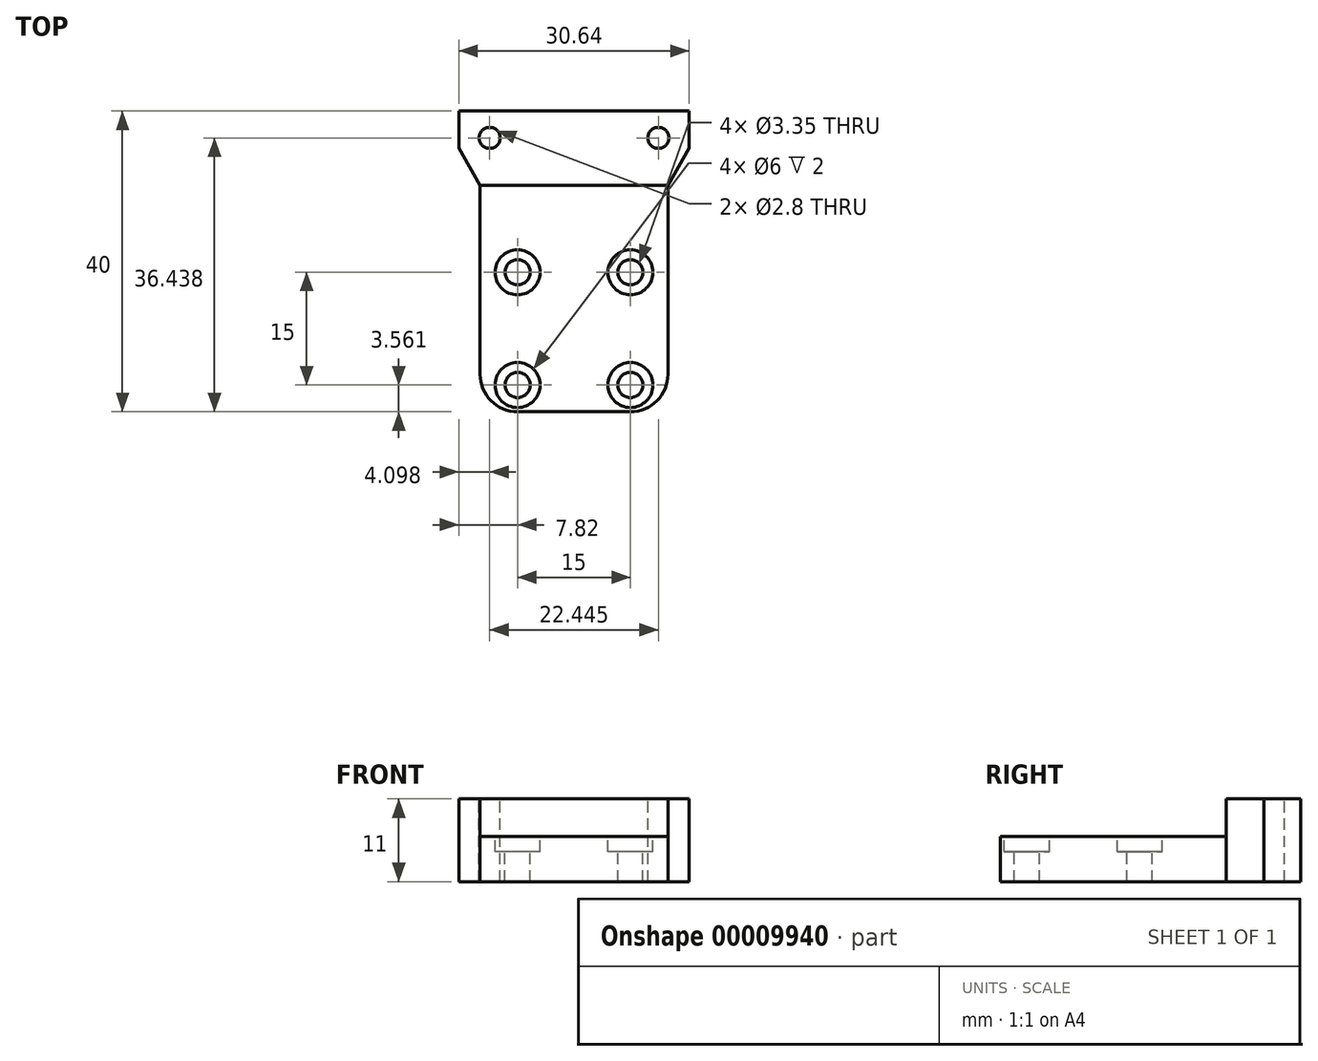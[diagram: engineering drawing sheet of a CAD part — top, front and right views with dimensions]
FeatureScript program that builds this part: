
annotation { "Feature Type Name" : "Feature", "Feature Type Description" : "" }
export const myFeature = defineFeature(function(context is Context, id is Id, definition is map)
    precondition{}
    {
        {
            var Q0;
            Q0=qCreatedBy(makeId("Top.planeOp"),FACE);
            var sketch = newSketch(context, id + "F0", { "sketchPlane" : qUnion([Q0])});
            skLineSegment(sketch, "E0.bottom", {"start": v(0, 0) * mm, "end": v(25, 0) * mm});
            skLineSegment(sketch, "E0.top", {"start": v(-2.82, 40) * mm, "end": v(27.82, 40) * mm});
            skLineSegment(sketch, "E1", {"start": v(0, 30.1) * mm, "end": v(25, 30.1) * mm});
            skLineSegment(sketch, "E2", {"start": v(-2.82, 35.1) * mm, "end": v(27.82, 35.1) * mm});
            skLineSegment(sketch, "E3", {"start": v(0, 0) * mm, "end": v(0, 30.1) * mm});
            skLineSegment(sketch, "E4", {"start": v(0, 30.1) * mm, "end": v(-2.82, 35.1) * mm});
            skLineSegment(sketch, "E5", {"start": v(-2.82, 35.1) * mm, "end": v(-2.82, 40) * mm});
            skLineSegment(sketch, "E6", {"start": v(25, 0) * mm, "end": v(25, 30.1) * mm});
            skLineSegment(sketch, "E7", {"start": v(25, 30.1) * mm, "end": v(27.82, 35.1) * mm});
            skLineSegment(sketch, "E8", {"start": v(27.82, 35.1) * mm, "end": v(27.82, 40) * mm});
            skSolve(sketch);
        }
        {
            var Q0;
            Q0=qSketchRegion(id+"F0",true);
            extrude(context, id + "F1", {"entities" : qUnion([Q0]), "depth" : 6 * mm});
        }
        {
            var Q0;
            Q0=makeQuery(id+"F1.opExtrude","CAP_FACE",FACE,{"disambiguationData":[OSD([sQuery(id+"F0.wireOp",EDGE,"E0.bottom"),sQuery(id+"F0.wireOp",EDGE,"E0.top"),sQuery(id+"F0.wireOp",EDGE,"E3"),sQuery(id+"F0.wireOp",EDGE,"E4"),sQuery(id+"F0.wireOp",EDGE,"E5"),sQuery(id+"F0.wireOp",EDGE,"E6"),sQuery(id+"F0.wireOp",EDGE,"E7"),sQuery(id+"F0.wireOp",EDGE,"E8")])],"isStart":false});
            var sketch = newSketch(context, id + "F2", { "sketchPlane" : qUnion([Q0])});
            skCircle(sketch, "E9", {"center": v(5, 18.56) * mm, "radius": 1.68 * mm});
            skCircle(sketch, "E10", {"center": v(20, 18.56) * mm, "radius": 1.68 * mm});
            skCircle(sketch, "E11", {"center": v(5, 3.56) * mm, "radius": 1.68 * mm});
            skCircle(sketch, "E12", {"center": v(20, 3.56) * mm, "radius": 1.68 * mm});
            skLineSegment(sketch, "E13", {"start": v(5, 18.56) * mm, "end": v(0, 18.56) * mm});
            skLineSegment(sketch, "E14", {"start": v(20, 3.56) * mm, "end": v(25, 3.56) * mm});
            skCircle(sketch, "E15", {"center": v(5, 18.56) * mm, "radius": 3 * mm});
            skCircle(sketch, "E16", {"center": v(20, 18.56) * mm, "radius": 3 * mm});
            skCircle(sketch, "E17", {"center": v(5, 3.56) * mm, "radius": 3 * mm});
            skCircle(sketch, "E18", {"center": v(20, 3.56) * mm, "radius": 3 * mm});
            skSolve(sketch);
        }
        {
            var Q0;
            Q0=makeQuery(id+"F2.imprint","IMPRINT",FACE,{"disambiguationData":[TD([[makeQuery(id+"F2.imprint","IMPRINT",EDGE,{"derivedFrom":sQuery(id+"F2.wireOp",EDGE,"E9")}),1.0]])]});
            var Q1;
            Q1=makeQuery(id+"F2.imprint","IMPRINT",FACE,{"disambiguationData":[TD([[makeQuery(id+"F2.imprint","IMPRINT",EDGE,{"derivedFrom":sQuery(id+"F2.wireOp",EDGE,"E10")}),1.0]])]});
            var Q2;
            Q2=makeQuery(id+"F2.imprint","IMPRINT",FACE,{"disambiguationData":[TD([[makeQuery(id+"F2.imprint","IMPRINT",EDGE,{"derivedFrom":sQuery(id+"F2.wireOp",EDGE,"E12")}),1.0]])]});
            var Q3;
            Q3=makeQuery(id+"F2.imprint","IMPRINT",FACE,{"disambiguationData":[TD([[makeQuery(id+"F2.imprint","IMPRINT",EDGE,{"derivedFrom":sQuery(id+"F2.wireOp",EDGE,"E11")}),1.0]])]});
            var Q4;
            Q4=makeQuery(id+"F2.imprint","IMPRINT",FACE,{"disambiguationData":[TD([[makeQuery(id+"F2.imprint","IMPRINT",EDGE,{"derivedFrom":sQuery(id+"F2.wireOp",EDGE,"97d24b09-4827-4c46-a1fd-a3ea8677536d")}),1.0]])]});
            var Q5;
            Q5=makeQuery(id+"F2.imprint","IMPRINT",FACE,{"disambiguationData":[TD([[makeQuery(id+"F2.imprint","IMPRINT",EDGE,{"derivedFrom":sQuery(id+"F2.wireOp",EDGE,"b6eb7b6f-8bb0-4363-9520-a6d7085f5256")}),1.0]])]});
            extrude(context, id + "F3", {"entities" : qUnion([Q0, Q1, Q2, Q3, Q4, Q5]), "operationType" : NewBodyOperationType.REMOVE, "oppositeDirection" : true, "depth" : 25 * mm});
        }
        {
            var Q0;
            Q0=makeQuery(id+"F2.imprint","IMPRINT",FACE,{"disambiguationData":[TD([[makeQuery(id+"F2.imprint","IMPRINT",EDGE,{"derivedFrom":sQuery(id+"F2.wireOp",EDGE,"E9")}),-1.0]])]});
            var Q1;
            Q1=makeQuery(id+"F2.imprint","IMPRINT",FACE,{"disambiguationData":[TD([[makeQuery(id+"F2.imprint","IMPRINT",EDGE,{"derivedFrom":sQuery(id+"F2.wireOp",EDGE,"E10")}),-1.0]])]});
            var Q2;
            Q2=makeQuery(id+"F2.imprint","IMPRINT",FACE,{"disambiguationData":[TD([[makeQuery(id+"F2.imprint","IMPRINT",EDGE,{"derivedFrom":sQuery(id+"F2.wireOp",EDGE,"E12")}),-1.0]])]});
            var Q3;
            Q3=makeQuery(id+"F2.imprint","IMPRINT",FACE,{"disambiguationData":[TD([[makeQuery(id+"F2.imprint","IMPRINT",EDGE,{"derivedFrom":sQuery(id+"F2.wireOp",EDGE,"E11")}),-1.0]])]});
            extrude(context, id + "F4", {"entities" : qUnion([Q0, Q1, Q2, Q3]), "operationType" : NewBodyOperationType.REMOVE, "oppositeDirection" : true, "depth" : 2 * mm});
        }
        {
            var Q0;
            Q0=makeQuery(id+"F1.opExtrude","SWEPT_EDGE",EDGE,{"disambiguationData":[OSD([sQuery(id+"F0.wireOp",EDGE,"E0.bottom"),sQuery(id+"F0.wireOp",EDGE,"E0.left")])]});
            var Q1;
            Q1=makeQuery(id+"F1.opExtrude","SWEPT_EDGE",EDGE,{"disambiguationData":[OSD([sQuery(id+"F0.wireOp",EDGE,"E0.bottom"),sQuery(id+"F0.wireOp",EDGE,"E0.right")])]});
            fillet(context, id + "F5", {"entities" : qUnion([Q0, Q1]), "radius" : 5 * mm, "tangentPropagation" : true, "allowEdgeOverflow" : false});
        }
        {
            var Q0;
            Q0=makeQuery(id+"F0.imprint","IMPRINT",FACE,{"disambiguationData":[TD([[makeQuery(id+"F0.imprint","IMPRINT",EDGE,{"derivedFrom":sQuery(id+"F0.wireOp",EDGE,"E0.top")}),-1.0]])]});
            var Q1;
            Q1=makeQuery(id+"F0.imprint","IMPRINT",FACE,{"disambiguationData":[TD([[makeQuery(id+"F0.imprint","IMPRINT",EDGE,{"derivedFrom":sQuery(id+"F0.wireOp",EDGE,"E1")}),1.0]])]});
            extrude(context, id + "F6", {"entities" : qUnion([Q0, Q1]), "operationType" : NewBodyOperationType.ADD, "depth" : 11 * mm});
        }
        {
            var Q0;
            Q0=makeQuery(id+"F6.opExtrude","CAP_FACE",FACE,{"disambiguationData":[OSD([sQuery(id+"F0.wireOp",EDGE,"E0.top"),sQuery(id+"F0.wireOp",EDGE,"E1"),sQuery(id+"F0.wireOp",EDGE,"E4"),sQuery(id+"F0.wireOp",EDGE,"E5"),sQuery(id+"F0.wireOp",EDGE,"E7"),sQuery(id+"F0.wireOp",EDGE,"E8")])],"isStart":false});
            var sketch = newSketch(context, id + "F7", { "sketchPlane" : qUnion([Q0])});
            skCircle(sketch, "E19", {"center": v(23.72, 36.44) * mm, "radius": 1.4 * mm});
            skCircle(sketch, "E20", {"center": v(1.28, 36.44) * mm, "radius": 1.4 * mm});
            skLineSegment(sketch, "E21", {"start": v(1.28, 36.44) * mm, "end": v(-2.82, 36.44) * mm});
            skLineSegment(sketch, "E22", {"start": v(23.72, 36.44) * mm, "end": v(27.82, 36.44) * mm});
            skSolve(sketch);
        }
        {
            var Q0;
            Q0 = qSketchRegion(id + "F7", true);
            extrude(context, id + "F8", {"entities" : qUnion([Q0]), "operationType" : NewBodyOperationType.REMOVE, "endBound" : BoundingType.THROUGH_ALL, "oppositeDirection" : true, "depth" : 25 * mm});
        }
    });
